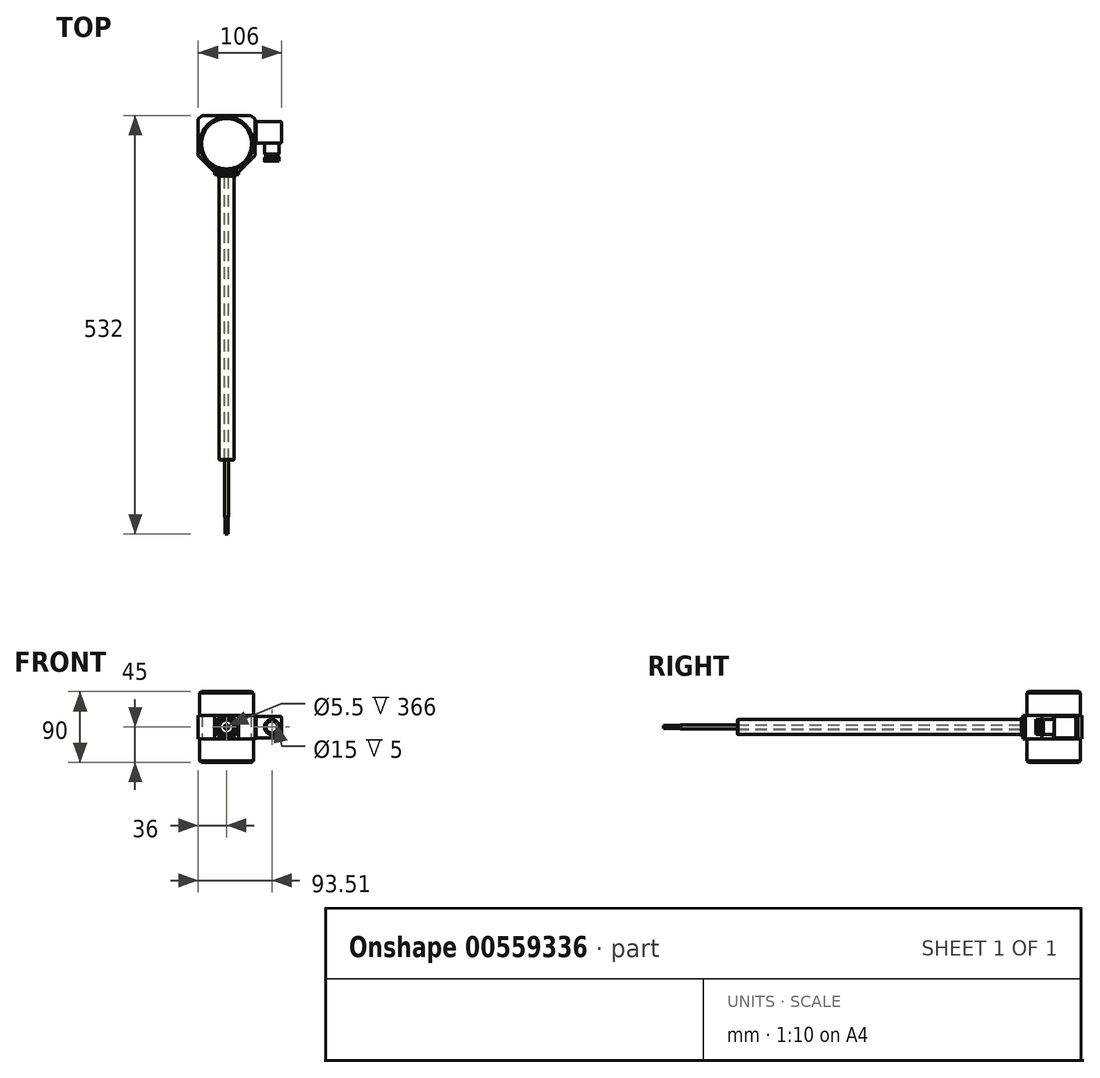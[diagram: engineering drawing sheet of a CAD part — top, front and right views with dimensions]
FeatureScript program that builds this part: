
annotation { "Feature Type Name" : "Feature", "Feature Type Description" : "" }
export const myFeature = defineFeature(function(context is Context, id is Id, definition is map)
    precondition{}
    {
        {
            var Q0;
            Q0=qCreatedBy(makeId("Front.planeOp"),FACE);
            var sketch = newSketch(context, id + "F0", { "sketchPlane" : qUnion([Q0])});
            skCircle(sketch, "E0", {"center": v(0, 0) * mm, "radius": 9.5 * mm});
            skCircle(sketch, "E1", {"center": v(0, 0) * mm, "radius": 2.75 * mm});
            skSolve(sketch);
        }
        {
            var Q0;
            Q0=makeQuery(id+"F0.imprint","IMPRINT",FACE,{"disambiguationData":[TD([[makeQuery(id+"F0.imprint","IMPRINT",EDGE,{"derivedFrom":sQuery(id+"F0.wireOp",EDGE,"E0")}),1.0]])]});
            extrude(context, id + "F1", {"entities" : qUnion([Q0]), "depth" : 361 * mm, "offsetDistance" : 25 * mm});
        }
        {
            var Q0;
            Q0=qCreatedBy(makeId("Front.planeOp"),FACE);
            var sketch = newSketch(context, id + "F2", { "sketchPlane" : qUnion([Q0])});
            skCircle(sketch, "E2", {"center": v(0, 0) * mm, "radius": 2.5 * mm});
            skSolve(sketch);
        }
        {
            var Q0;
            Q0=makeQuery(id+"F2.imprint","IMPRINT",FACE,{"disambiguationData":[TD([[makeQuery(id+"F2.imprint","IMPRINT",EDGE,{"derivedFrom":sQuery(id+"F2.wireOp",EDGE,"E2")}),1.0]])]});
            extrude(context, id + "F3", {"entities" : qUnion([Q0]), "depth" : (455 - 22) * mm, "offsetDistance" : 25 * mm});
        }
        {
            var Q0;
            Q0=makeQuery(id+"F3.opExtrude","CAP_FACE",FACE,{"disambiguationData":[OSD([sQuery(id+"F2.wireOp",EDGE,"E2")])],"isStart":false});
            var sketch = newSketch(context, id + "F4", { "sketchPlane" : qUnion([Q0])});
            skCircle(sketch, "E3", {"center": v(0, 0) * mm, "radius": 2.1 * mm});
            skSolve(sketch);
        }
        {
            var Q0;
            Q0=makeQuery(id+"F4.imprint","IMPRINT",FACE,{"disambiguationData":[TD([[makeQuery(id+"F4.imprint","IMPRINT",EDGE,{"derivedFrom":sQuery(id+"F4.wireOp",EDGE,"E3")}),1.0]])]});
            extrude(context, id + "F5", {"entities" : qUnion([Q0]), "operationType" : NewBodyOperationType.ADD, "depth" : 22 * mm, "offsetDistance" : 25 * mm});
        }
        {
            var Q0;
            Q0=makeQuery(id+"F1.opExtrude","CAP_EDGE",EDGE,{"disambiguationData":[OSD([sQuery(id+"F0.wireOp",EDGE,"E0")])],"isStart":false});
            chamfer(context, id + "F6", {"entities" : qUnion([Q0]), "width" : 0.6 * mm, "tangentPropagation" : true});
        }
        {
            var Q0;
            Q0=makeQuery(id+"F1.opExtrude","CAP_FACE",FACE,{"disambiguationData":[OSD([sQuery(id+"F0.wireOp",EDGE,"E0"),sQuery(id+"F0.wireOp",EDGE,"E1")])],"isStart":true});
            var sketch = newSketch(context, id + "F7", { "sketchPlane" : qUnion([Q0])});
            skCircle(sketch, "E4", {"center": v(0, 0) * mm, "radius": 12 * mm});
            skSolve(sketch);
        }
        {
            var Q0;
            Q0=makeQuery(id+"F7.imprint","IMPRINT",FACE,{"disambiguationData":[TD([[makeQuery(id+"F7.imprint","IMPRINT",EDGE,{"derivedFrom":makeQuery(id+"F1.opExtrude","CAP_EDGE",EDGE,{"disambiguationData":[OSD([sQuery(id+"F0.wireOp",EDGE,"E0")])],"isStart":true})}),-1.0]])]});
            var Q1;
            Q1=makeQuery(id+"F7.imprint","IMPRINT",FACE,{"disambiguationData":[TD([[makeQuery(id+"F7.imprint","IMPRINT",EDGE,{"derivedFrom":sQuery(id+"F7.wireOp",EDGE,"E4")}),1.0]])]});
            extrude(context, id + "F8", {"entities" : qUnion([Q0, Q1]), "operationType" : NewBodyOperationType.ADD, "depth" : 2 * mm, "offsetDistance" : 25 * mm});
        }
        {
            var Q0;
            Q0=makeQuery(id+"F8.opExtrude","CAP_FACE",FACE,{"disambiguationData":[OSD([sQuery(id+"F0.wireOp",EDGE,"E1"),sQuery(id+"F7.wireOp",EDGE,"E4")])],"isStart":false});
            var sketch = newSketch(context, id + "F9", { "sketchPlane" : qUnion([Q0])});
            skCircle(sketch, "E5", {"center": v(0, 0) * mm, "radius": 15 * mm});
            skSolve(sketch);
        }
        {
            var Q0;
            Q0=makeQuery(id+"F9.imprint","IMPRINT",FACE,{"disambiguationData":[TD([[makeQuery(id+"F9.imprint","IMPRINT",EDGE,{"derivedFrom":sQuery(id+"F9.wireOp",EDGE,"E5")}),1.0]])]});
            var Q1;
            Q1=makeQuery(id+"F9.imprint","IMPRINT",FACE,{"disambiguationData":[TD([[makeQuery(id+"F9.imprint","IMPRINT",EDGE,{"derivedFrom":makeQuery(id+"F8.opExtrude","CAP_EDGE",EDGE,{"disambiguationData":[OSD([sQuery(id+"F7.wireOp",EDGE,"E4")])],"isStart":false})}),1.0]])]});
            extrude(context, id + "F10", {"entities" : qUnion([Q0, Q1]), "operationType" : NewBodyOperationType.ADD, "depth" : 3 * mm, "offsetDistance" : 25 * mm});
        }
        {
            var Q0;
            Q0=qCreatedBy(makeId("Top.planeOp"),FACE);
            var sketch = newSketch(context, id + "F11", { "sketchPlane" : qUnion([Q0])});
            skLineSegment(sketch, "E6", {"start": v(54.6, 41) * mm, "end": v(-46.81, 41) * mm, "construction": true});
            skCircle(sketch, "E7", {"center": v(0, 41) * mm, "radius": 34 * mm});
            skLineSegment(sketch, "E8", {"start": v(15, 5) * mm, "end": v(36, 26) * mm});
            skLineSegment(sketch, "E9", {"start": v(36, 72) * mm, "end": v(31, 77) * mm});
            skLineSegment(sketch, "E10.trimOffspring", {"start": v(31, 77) * mm, "end": v(0, 77) * mm});
            skLineSegment(sketch, "E11.trimOffspring", {"start": v(36, 72) * mm, "end": v(36, 26) * mm});
            skLineSegment(sketch, "E12", {"start": v(15, 5) * mm, "end": v(0, 5) * mm});
            skLineSegment(sketch, "E13", {"start": v(0, 5) * mm, "end": v(0, 77) * mm, "construction": true});
            skLineSegment(sketch, "E14.MirrorCS", {"start": v(-15, 5) * mm, "end": v(-36, 26) * mm});
            skLineSegment(sketch, "E15.MirrorCS", {"start": v(-15, 5) * mm, "end": v(0, 5) * mm});
            skLineSegment(sketch, "E16.MirrorCS", {"start": v(-36, 72) * mm, "end": v(-36, 26) * mm});
            skLineSegment(sketch, "E17.MirrorCS", {"start": v(-31, 77) * mm, "end": v(0, 77) * mm});
            skLineSegment(sketch, "E18.MirrorCS", {"start": v(-36, 72) * mm, "end": v(-31, 77) * mm});
            skSolve(sketch);
        }
        {
            var Q0;
            Q0=makeQuery(id+"F11.imprint","IMPRINT",FACE,{"disambiguationData":[TD([[makeQuery(id+"F11.imprint","IMPRINT",EDGE,{"derivedFrom":sQuery(id+"F11.wireOp",EDGE,"E8")}),1.0]])]});
            extrude(context, id + "F12", {"entities" : qUnion([Q0]), "operationType" : NewBodyOperationType.ADD, "endBound" : BoundingType.SYMMETRIC, "depth" : 30 * mm, "offsetDistance" : 25 * mm});
        }
        {
            var Q0;
            Q0=makeQuery(id+"F11.imprint","IMPRINT",FACE,{"disambiguationData":[TD([[makeQuery(id+"F11.imprint","IMPRINT",EDGE,{"derivedFrom":sQuery(id+"F11.wireOp",EDGE,"E7")}),1.0]])]});
            extrude(context, id + "F13", {"entities" : qUnion([Q0]), "operationType" : NewBodyOperationType.ADD, "endBound" : BoundingType.SYMMETRIC, "depth" : 90 * mm, "offsetDistance" : 25 * mm});
        }
        {
            var Q0;
            Q0=makeQuery(id+"F13.opExtrude","CAP_EDGE",EDGE,{"disambiguationData":[OSD([sQuery(id+"F11.wireOp",EDGE,"E7")])],"isStart":false});
            var Q1;
            Q1=makeQuery(id+"F13.opExtrude","CAP_EDGE",EDGE,{"disambiguationData":[OSD([sQuery(id+"F11.wireOp",EDGE,"E7")])],"isStart":true});
            chamfer(context, id + "F14", {"entities" : qUnion([Q0, Q1]), "width" : 2 * mm, "tangentPropagation" : true});
        }
        {
            var Q0;
            Q0=makeQuery(id+"F12.opExtrude","SWEPT_FACE",FACE,{"disambiguationData":[OSD([sQuery(id+"F11.wireOp",EDGE,"E11.trimOffspring")])]});
            var sketch = newSketch(context, id + "F15", { "sketchPlane" : qUnion([Q0])});
            skLineSegment(sketch, "E19.bottom", {"start": v(67.15, -13.75) * mm, "end": v(43.65, -13.75) * mm});
            skLineSegment(sketch, "E19.top", {"start": v(67.15, 13.75) * mm, "end": v(43.65, 13.75) * mm});
            skLineSegment(sketch, "E19.left", {"start": v(69.15, -11.75) * mm, "end": v(69.15, 11.75) * mm});
            skLineSegment(sketch, "E19.right", {"start": v(41.65, -11.75) * mm, "end": v(41.65, 11.75) * mm});
            skPoint(sketch, "E19.middle", {"position": v(55.4, 0) * mm});
            skPoint(sketch, "E20.visualSharp", {"position": v(69.15, 13.75) * mm});
            skArc(sketch, "E20.filletArc", {"start": v(69.15, 11.75) * mm, "mid": v(68.56, 13.16) * mm, "end": v(67.15, 13.75) * mm});
            skPoint(sketch, "E21.visualSharp", {"position": v(69.15, -13.75) * mm});
            skArc(sketch, "E21.filletArc", {"start": v(67.15, -13.75) * mm, "mid": v(68.56, -13.16) * mm, "end": v(69.15, -11.75) * mm});
            skPoint(sketch, "E22.visualSharp", {"position": v(41.65, -13.75) * mm});
            skArc(sketch, "E22.filletArc", {"start": v(41.65, -11.75) * mm, "mid": v(42.23, -13.16) * mm, "end": v(43.65, -13.75) * mm});
            skPoint(sketch, "E23.visualSharp", {"position": v(41.65, 13.75) * mm});
            skArc(sketch, "E23.filletArc", {"start": v(43.65, 13.75) * mm, "mid": v(42.23, 13.16) * mm, "end": v(41.65, 11.75) * mm});
            skArc(sketch, "E24.0", {"start": v(40.65, -11.75) * mm, "mid": v(41.53, -13.87) * mm, "end": v(43.65, -14.75) * mm});
            skLineSegment(sketch, "E24.1", {"start": v(67.15, -14.75) * mm, "end": v(43.65, -14.75) * mm});
            skLineSegment(sketch, "E24.2", {"start": v(40.65, -11.75) * mm, "end": v(40.65, 11.75) * mm});
            skArc(sketch, "E24.3", {"start": v(67.15, -14.75) * mm, "mid": v(69.27, -13.87) * mm, "end": v(70.15, -11.75) * mm});
            skArc(sketch, "E24.4", {"start": v(43.65, 14.75) * mm, "mid": v(41.53, 13.87) * mm, "end": v(40.65, 11.75) * mm});
            skLineSegment(sketch, "E24.5", {"start": v(67.15, 14.75) * mm, "end": v(43.65, 14.75) * mm});
            skArc(sketch, "E24.6", {"start": v(70.15, 11.75) * mm, "mid": v(69.27, 13.87) * mm, "end": v(67.15, 14.75) * mm});
            skLineSegment(sketch, "E24.7", {"start": v(70.15, -11.75) * mm, "end": v(70.15, 11.75) * mm});
            skSolve(sketch);
        }
        {
            var Q0;
            Q0=makeQuery(id+"F15.imprint","IMPRINT",FACE,{"disambiguationData":[TD([[makeQuery(id+"F15.imprint","IMPRINT",EDGE,{"derivedFrom":sQuery(id+"F15.wireOp",EDGE,"E19.bottom")}),1.0]])]});
            var Q1;
            Q1=makeQuery(id+"F15.imprint","IMPRINT",FACE,{"disambiguationData":[TD([[makeQuery(id+"F15.imprint","IMPRINT",EDGE,{"derivedFrom":sQuery(id+"F15.wireOp",EDGE,"E19.bottom")}),-1.0]])]});
            var Q2;
            Q2=sQuery(id+"F15.wireOp",EDGE,"E24.5");
            var Q3;
            Q3=sQuery(id+"F15.wireOp",EDGE,"E24.6");
            var Q4;
            Q4=sQuery(id+"F15.wireOp",EDGE,"E24.7");
            var Q5;
            Q5=sQuery(id+"F15.wireOp",EDGE,"E24.3");
            var Q6;
            Q6=sQuery(id+"F15.wireOp",EDGE,"E24.1");
            var Q7;
            Q7=sQuery(id+"F15.wireOp",EDGE,"E24.0");
            var Q8;
            Q8=sQuery(id+"F15.wireOp",EDGE,"E24.2");
            var Q9;
            Q9=sQuery(id+"F15.wireOp",EDGE,"E24.4");
            extrude(context, id + "F16", {"entities" : qUnion([Q0, Q1]), "operationType" : NewBodyOperationType.ADD, "surfaceEntities" : qUnion([Q2, Q3, Q4, Q5, Q6, Q7, Q8, Q9]), "depth" : 1.5 * mm, "offsetDistance" : 25 * mm});
        }
        {
            var Q0;
            Q0=makeQuery(id+"F15.imprint","IMPRINT",FACE,{"disambiguationData":[TD([[makeQuery(id+"F15.imprint","IMPRINT",EDGE,{"derivedFrom":sQuery(id+"F15.wireOp",EDGE,"E19.bottom")}),-1.0]])]});
            extrude(context, id + "F17", {"entities" : qUnion([Q0]), "operationType" : NewBodyOperationType.ADD, "depth" : 34 * mm, "offsetDistance" : 25 * mm});
        }
        {
            var Q0;
            Q0=makeQuery(id+"F17.opExtrude","CAP_FACE",FACE,{"disambiguationData":[OSD([sQuery(id+"F15.wireOp",EDGE,"E19.bottom"),sQuery(id+"F15.wireOp",EDGE,"E19.top"),sQuery(id+"F15.wireOp",EDGE,"E19.left"),sQuery(id+"F15.wireOp",EDGE,"E19.right"),sQuery(id+"F15.wireOp",EDGE,"E20.filletArc"),sQuery(id+"F15.wireOp",EDGE,"E21.filletArc"),sQuery(id+"F15.wireOp",EDGE,"E22.filletArc"),sQuery(id+"F15.wireOp",EDGE,"E23.filletArc")])],"isStart":false});
            fillet(context, id + "F18", {"entities" : qUnion([Q0]), "radius" : 2 * mm, "tangentPropagation" : true, "allowEdgeOverflow" : false});
        }
        {
            var Q0;
            Q0=makeQuery(id+"F17.opExtrude","SWEPT_FACE",FACE,{"disambiguationData":[OSD([sQuery(id+"F15.wireOp",EDGE,"E19.right")])]});
            var sketch = newSketch(context, id + "F19", { "sketchPlane" : qUnion([Q0])});
            skCircle(sketch, "E25", {"center": v(57.51, 0) * mm, "radius": 9.5 * mm});
            skSolve(sketch);
        }
        {
            var Q0;
            Q0=makeQuery(id+"F19.imprint","IMPRINT",FACE,{"disambiguationData":[TD([[makeQuery(id+"F19.imprint","IMPRINT",EDGE,{"derivedFrom":sQuery(id+"F19.wireOp",EDGE,"E25")}),1.0]])]});
            extrude(context, id + "F20", {"entities" : qUnion([Q0]), "operationType" : NewBodyOperationType.ADD, "depth" : (41 - 27) * mm, "offsetDistance" : 25 * mm});
        }
        {
            var Q0;
            Q0=makeQuery(id+"F20.opExtrude","CAP_FACE",FACE,{"disambiguationData":[OSD([sQuery(id+"F19.wireOp",EDGE,"E25")])],"isStart":false});
            var sketch = newSketch(context, id + "F21", { "sketchPlane" : qUnion([Q0])});
            skCircle(sketch, "E26", {"center": v(57.51, 0) * mm, "radius": 8 * mm});
            skSolve(sketch);
        }
        {
            var Q0;
            Q0=makeQuery(id+"F21.imprint","IMPRINT",FACE,{"disambiguationData":[TD([[makeQuery(id+"F21.imprint","IMPRINT",EDGE,{"derivedFrom":sQuery(id+"F21.wireOp",EDGE,"E26")}),1.0]])]});
            extrude(context, id + "F22", {"entities" : qUnion([Q0]), "operationType" : NewBodyOperationType.ADD, "depth" : 4 * mm, "offsetDistance" : 25 * mm});
        }
        {
            var Q0;
            Q0=makeQuery(id+"F22.opExtrude","CAP_FACE",FACE,{"disambiguationData":[OSD([sQuery(id+"F21.wireOp",EDGE,"E26")])],"isStart":false});
            var sketch = newSketch(context, id + "F23", { "sketchPlane" : qUnion([Q0])});
            skArc(sketch, "E27.0", {"start": v(66.83, 1.82) * mm, "mid": v(66.69, 2.46) * mm, "end": v(66.5, 3.09) * mm});
            skLineSegment(sketch, "E28", {"start": v(57.51, 0) * mm, "end": v(67.6, 0) * mm, "construction": true});
            skLineSegment(sketch, "E29", {"start": v(57.51, 0) * mm, "end": v(66.65, 5.27) * mm, "construction": true});
            skArc(sketch, "E30", {"start": v(65.51, 0) * mm, "mid": v(66.77, 2.48) * mm, "end": v(64.44, 4) * mm});
            skPoint(sketch, "E30.first.point", {"position": v(64.44, 4) * mm});
            skPoint(sketch, "E30.second.point", {"position": v(65.51, 0) * mm});
            skPoint(sketch, "E30.third.point", {"position": v(66.83, 1.82) * mm});
            skArc(sketch, "E31.1.0", {"start": v(64.44, -4) * mm, "mid": v(66.77, -2.48) * mm, "end": v(65.51, 0) * mm});
            skArc(sketch, "E31.2.0", {"start": v(61.51, -6.93) * mm, "mid": v(64.29, -6.78) * mm, "end": v(64.44, -4) * mm});
            skArc(sketch, "E31.3.0", {"start": v(57.51, -8) * mm, "mid": v(60, -9.26) * mm, "end": v(61.51, -6.93) * mm});
            skArc(sketch, "E31.4.0", {"start": v(53.51, -6.93) * mm, "mid": v(55.03, -9.26) * mm, "end": v(57.51, -8) * mm});
            skArc(sketch, "E31.5.0", {"start": v(50.58, -4) * mm, "mid": v(50.73, -6.78) * mm, "end": v(53.51, -6.93) * mm});
            skArc(sketch, "E31.6.0", {"start": v(49.51, 0) * mm, "mid": v(48.25, -2.48) * mm, "end": v(50.58, -4) * mm});
            skArc(sketch, "E31.7.0", {"start": v(50.58, 4) * mm, "mid": v(48.25, 2.48) * mm, "end": v(49.51, 0) * mm});
            skArc(sketch, "E31.8.0", {"start": v(53.51, 6.93) * mm, "mid": v(50.73, 6.78) * mm, "end": v(50.58, 4) * mm});
            skArc(sketch, "E31.9.0", {"start": v(57.51, 8) * mm, "mid": v(55.03, 9.26) * mm, "end": v(53.51, 6.93) * mm});
            skArc(sketch, "E31.10.0", {"start": v(61.51, 6.93) * mm, "mid": v(60, 9.26) * mm, "end": v(57.51, 8) * mm});
            skArc(sketch, "E31.11.0", {"start": v(64.44, 4) * mm, "mid": v(64.29, 6.78) * mm, "end": v(61.51, 6.93) * mm});
            skLineSegment(sketch, "E31.anchor1", {"start": v(57.51, 0) * mm, "end": v(65.51, 0) * mm, "construction": true});
            skLineSegment(sketch, "E31.anchor2", {"start": v(57.51, 0) * mm, "end": v(64.44, 4) * mm, "construction": true});
            skCircle(sketch, "E32", {"center": v(57.51, 0) * mm, "radius": 7.5 * mm});
            skSolve(sketch);
        }
        {
            var Q0;
            Q0 = qSketchRegion(id + "F23", true);
            extrude(context, id + "F24", {"entities" : qUnion([Q0]), "operationType" : NewBodyOperationType.ADD, "depth" : 5 * mm, "offsetDistance" : 25 * mm});
        }
    });
